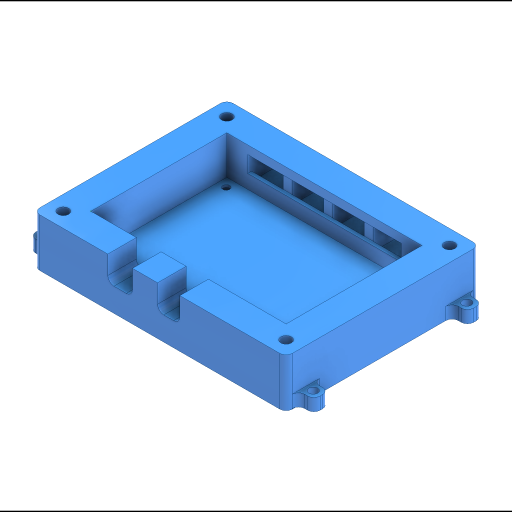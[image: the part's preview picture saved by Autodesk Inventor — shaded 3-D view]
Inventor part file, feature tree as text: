
AUTODESK INVENTOR PART (.ipt)
format: ipt  version: 2023 (Build 270158000, 158)  size: 813,056 bytes
history: native  units: in
note: dims shown in document units (in); Inventor stores cm internally (conversion verified against a paired STEP export)
features: sketch x17, extrude x16, projected_geometry x6, fillet x3
ambient origin geometry x8: Origin, YZ Plane, XZ Plane, XY Plane, X Axis, Y Axis, Z Axis, Center Point
bodies: Solid1 (feature_tree)
feature tree (42):
  extrude  "Extrusion1"  Depth=2.75in
  extrude  "Extrusion2"  Depth=0.0787in
  extrude  "Extrusion3"  Depth=0.0787in
  extrude  "Extrusion4"  Depth=0.1969in TaperAngle=0.0deg
  extrude  "Extrusion5"  Depth=0.3in
  extrude  "Extrusion6"  Depth=0.3in
  extrude  "Extrusion7"  Depth=2.375in
  extrude  "Extrusion12"  Depth=3.625in
  extrude  "Extrusion13"  Depth=0.2512in
  extrude  "Extrusion14"  Depth=0.27in
  extrude  "Extrusion16"  Depth=0.1496in
  sketch  "Sketch17"  dims[d26=0.14in d27=0.14in]
  extrude  "Extrusion17"  Depth=0.14in
  extrude  "Extrusion18"  TaperAngle=0.0deg  [1 undecoded]
  fillet  "Fillet3"  Radius=0.375in
  fillet  "Fillet4"  Radius=0.375in
  extrude  "Extrusion19"  Depth=0.375in
  extrude  "Extrusion20"  Depth=0.5in
  extrude  "Extrusion21"  Depth=0.5in
  fillet  "Fillet5"  Radius=1.0in
  sketch  "Sketch1"  dims[d0=3.95in d1=2.75in]
  sketch  "Sketch2"  dims[d3=0.0787in d4=0.0787in]
  projected_geometry  "Projected Loop1"
  sketch  "Sketch3"  dims[d5=0.0787in d6=0.0787in]
  sketch  "Sketch4"  dims[d7=0.28in d8=0.0in d9=0.1969in d10=0.0in]
  sketch  "Sketch5"  dims[d11=0.3in d12=0.3in]
  sketch  "Sketch6"  dims[d13=0.3in d14=0.3in]
  projected_geometry  "Projected Loop2"
  sketch  "Sketch7"  dims[d15=2.375in d16=2.375in]
  projected_geometry  "Projected Loop3"
  sketch  "Sketch12"  dims[d17=0.0in d18=3.625in]
  sketch  "Sketch13"  dims[d19=3.625in d20=0.2512in]
  projected_geometry  "Projected Loop8"
  sketch  "Sketch14"  dims[d21=0.251in d22=0.27in]
  projected_geometry  "Projected Loop9"
  sketch  "Sketch16"  dims[d23=0.1496in d24=0.0in d25=0.14in]
  projected_geometry  "Projected Loop11"
  sketch  "Sketch18"  dims[d28=0.14in d29=0.0in d30=0.0in d31=0.375in d32=0.375in]
  sketch  "Sketch19"  dims[d33=0.375in d34=0.375in]
  sketch  "Sketch20"  dims[d35=0.0in d36=0.0in d37=0.5in]
  sketch  "Sketch21"  dims[d38=0.5in d39=0.5in d40=1.0in]
  sketch  "Sketch22"  dims[d41=1.65in d42=0.45in d43=0.5in d44=0.0in d45=0.5in d46=0.0in d78=0.5in d79=0.0in d80=0.5in d81=0.0in d82=0.5in d83=0.0in d86=0.3in d87=0.5in d88=0.0in d89=0.17in d90=0.5in d91=0.0in d92=0.0925in d93=0.0925in d94=0.635in d95=0.185in d96=0.185in d97=0.635in d98=1.0in d99=0.0in d100=0.125in d101=0.125in d102=0.217in d103=0.217in d104=0.217in d105=0.217in d106=0.3in d107=0.3in d108=0.3in d109=0.3in d110=0.3in d111=0.3in d112=0.3in d113=0.3in d114=0.5in d115=0.0in d116=0.3in d117=0.25in d118=0.3in d119=0.25in d120=0.25in d121=0.25in d122=0.3125in d123=5.438in d124=0.0in d125=0.0in d126=0.15in d127=0.15in d128=0.15in d129=0.15in d130=0.18in d131=0.18in d132=0.18in d133=0.15in d134=0.15in d135=0.18in d136=0.15in d137=0.15in d138=0.0in d139=0.0in d140=0.125in]
note: 1 required parameter value undecoded (feature->parameter linkage not recoverable at this tier; creation-order binding heuristic only, values carry confidence <= 0.55)
